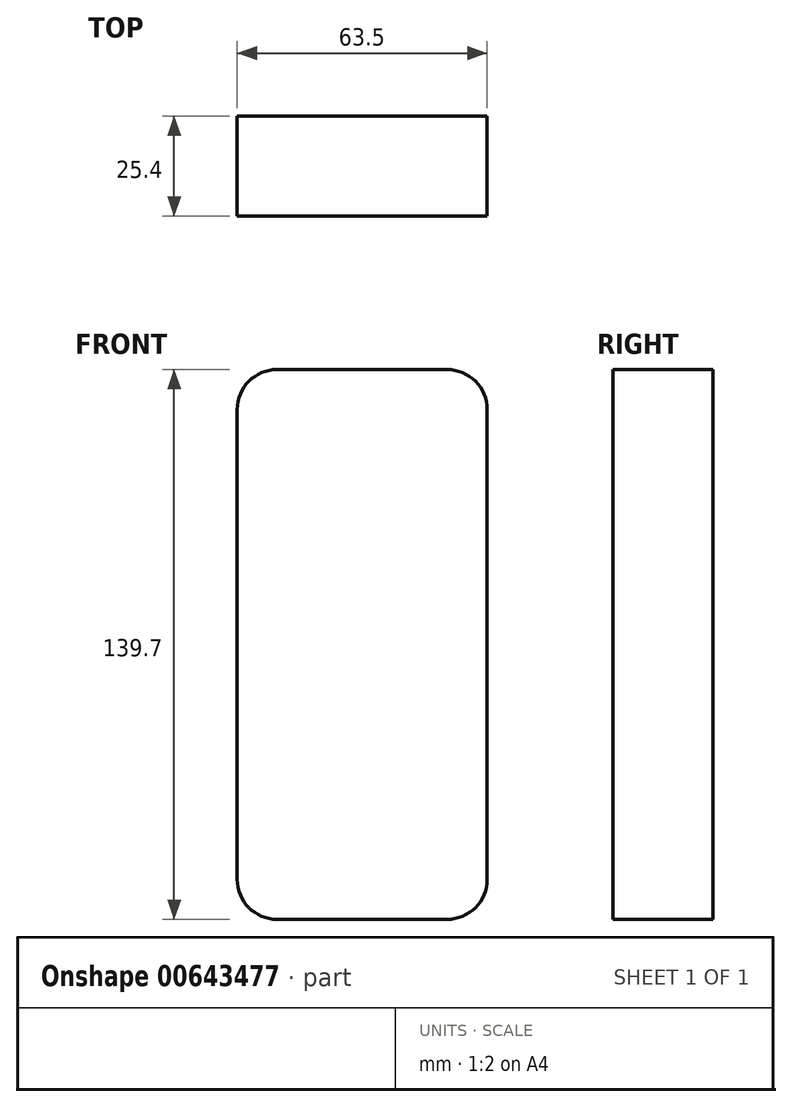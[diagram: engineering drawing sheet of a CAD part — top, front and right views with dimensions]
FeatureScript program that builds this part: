
annotation { "Feature Type Name" : "Feature", "Feature Type Description" : "" }
export const myFeature = defineFeature(function(context is Context, id is Id, definition is map)
    precondition{}
    {
        {
            var Q0;
            Q0=qCreatedBy(makeId("Front.planeOp"),FACE);
            var sketch = newSketch(context, id + "F0", { "sketchPlane" : qUnion([Q0])});
            skLineSegment(sketch, "E0.bottom", {"start": v(0, 0) * mm, "end": v(63.5, 0) * mm});
            skLineSegment(sketch, "E0.top", {"start": v(0, 139.7) * mm, "end": v(63.5, 139.7) * mm});
            skLineSegment(sketch, "E0.left", {"start": v(0, 0) * mm, "end": v(0, 139.7) * mm});
            skLineSegment(sketch, "E0.right", {"start": v(63.5, 0) * mm, "end": v(63.5, 139.7) * mm});
            skSolve(sketch);
        }
        {
            var Q0;
            Q0=makeQuery(id+"F0.imprint","IMPRINT",FACE,{"disambiguationData":[TD([[makeQuery(id+"F0.imprint","IMPRINT",EDGE,{"derivedFrom":sQuery(id+"F0.wireOp",EDGE,"E0.bottom")}),1.0]])]});
            extrude(context, id + "F1", {"entities" : qUnion([Q0]), "depth" : 25.4 * mm, "offsetDistance" : 25.4 * mm});
        }
        {
            var Q0;
            Q0=makeQuery(id+"F1.opExtrude","SWEPT_EDGE",EDGE,{"disambiguationData":[OSD([sQuery(id+"F0.wireOp",EDGE,"E0.top"),sQuery(id+"F0.wireOp",EDGE,"E0.left")])]});
            fillet(context, id + "F2", {"entities" : qUnion([Q0]), "radius" : 10.16 * mm, "tangentPropagation" : true, "allowEdgeOverflow" : false});
        }
        {
            var Q0;
            Q0=makeQuery(id+"F1.opExtrude","SWEPT_EDGE",EDGE,{"disambiguationData":[OSD([sQuery(id+"F0.wireOp",EDGE,"E0.bottom"),sQuery(id+"F0.wireOp",EDGE,"E0.left")])]});
            fillet(context, id + "F3", {"entities" : qUnion([Q0]), "radius" : 10.16 * mm, "tangentPropagation" : true, "allowEdgeOverflow" : false});
        }
        {
            var Q0;
            Q0=makeQuery(id+"F1.opExtrude","SWEPT_EDGE",EDGE,{"disambiguationData":[OSD([sQuery(id+"F0.wireOp",EDGE,"E0.top"),sQuery(id+"F0.wireOp",EDGE,"E0.right")])]});
            fillet(context, id + "F4", {"entities" : qUnion([Q0]), "radius" : 10.16 * mm, "tangentPropagation" : true, "allowEdgeOverflow" : false});
        }
        {
            var Q0;
            Q0=makeQuery(id+"F1.opExtrude","SWEPT_EDGE",EDGE,{"disambiguationData":[OSD([sQuery(id+"F0.wireOp",EDGE,"E0.bottom"),sQuery(id+"F0.wireOp",EDGE,"E0.right")])]});
            fillet(context, id + "F5", {"entities" : qUnion([Q0]), "radius" : 10.16 * mm, "tangentPropagation" : true, "allowEdgeOverflow" : false});
        }
    });
